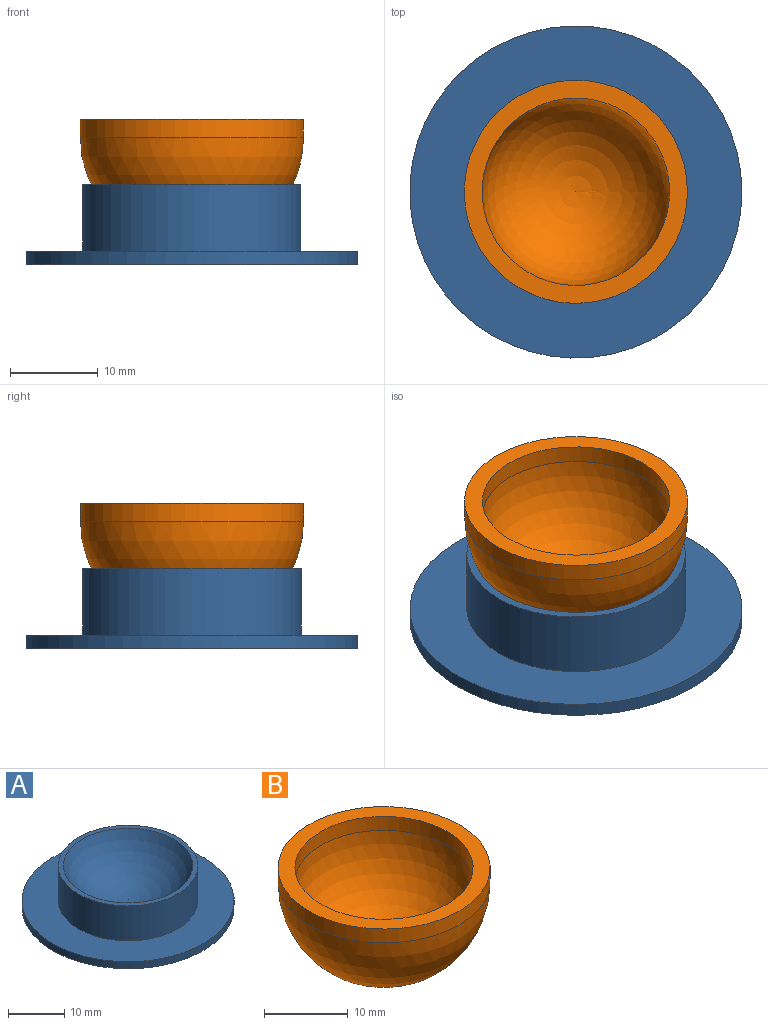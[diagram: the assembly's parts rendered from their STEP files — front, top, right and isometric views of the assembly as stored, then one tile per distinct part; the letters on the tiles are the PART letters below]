
ASSEMBLY  parts=2 mates=1
PART A: 6 faces, bbox 37.8x37.8x9.1 mm
  f0: cylinder r=18.9mm len=37.81mm, axis (0,0,1), area 181mm2, adj f1,f2
  f1: plane 37.81x37.81mm, normal (0,0,-1), area 1122.7mm2, adj f0
  f2: plane 37.81x37.81mm, normal (0,0,1), area 636mm2, adj f0,f3
  f3: cylinder r=12.45mm len=24.89mm, axis (0,0,-1), area 595.9mm2, adj f2,f4
  f4: plane 24.89x24.89mm, normal (0,0,1), area 69.3mm2, adj f3,f5
  f5: sphere r=12.7mm, area 587.8mm2, adj f4
PART B: 5 faces, bbox 25.4x25.4x14.7 mm
  f0: sphere r=10.67mm, area 715.1mm2, adj f4
  f1: sphere r=12.7mm, area 1013.4mm2, adj f2
  f2: cylinder r=12.7mm len=25.4mm, axis (0,0,1), area 162.1mm2, adj f1,f3
  f3: plane 25.4x25.4mm, normal (0,0,1), area 149.2mm2, adj f2,f4
  f4: cylinder r=10.67mm len=21.34mm, axis (0,0,1), area 136.2mm2, adj f0,f3
PLACE A t=(0.04,-0.06,-3.17)mm
PLACE B t=(0.04,-0.06,11.81)mm
MATE fastened B.f2 <-> A.f0  axis (0,0,1) through (0.04,-0.06,9.78)mm
